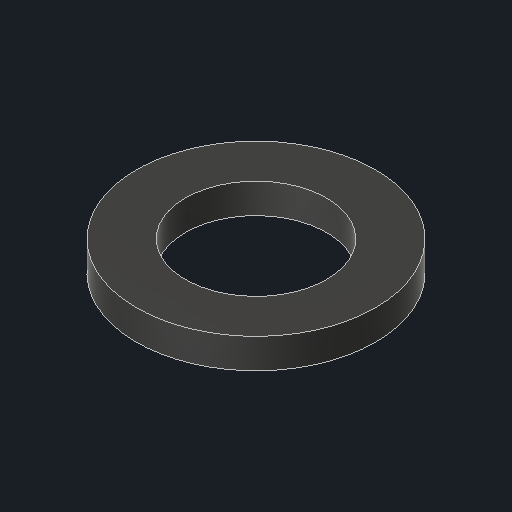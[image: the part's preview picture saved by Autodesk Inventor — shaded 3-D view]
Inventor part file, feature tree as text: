
AUTODESK INVENTOR PART (.ipt)
format: ipt  version: 2023 (Build 270158000, 158)  size: 814,592 bytes
history: native  units: in
note: dims shown in document units (in); Inventor stores cm internally (conversion verified against a paired STEP export)
features: other x39, sketch x4, extrude x3, thread x2, revolve x1, mirror x1
ambient origin geometry x8: Origin, YZ Plane, XZ Plane, XY Plane, X Axis, Y Axis, Z Axis, Center Point
bodies: Body1 (feature_tree)
feature tree (50):
  other  "Table"
  other  "Length = 2"
  other  "Length = 1.4375"
  other  "Length = 2.5"
  other  "Length = 1.75"
  other  "Spacer Type = Nylon Unthreaded Spacer"
  other  "Spacer Size = 4-40"
  other  "Length = 0.125"
  other  "Length = 0.15625"
  other  "Length = 0.1875"
  other  "Length = 0.21875"
  other  "Length = 0.25"
  other  "Length = 0.28125"
  other  "Length = 0.3125"
  other  "Length = 0.34375"
  other  "Length = 0.375"
  other  "Length = 0.40625"
  other  "Length = 0.4375"
  other  "Length = 0.46875"
  other  "Length = 0.5"
  other  "Length = 0.5625"
  other  "Length = 0.625"
  other  "Length = 0.6875"
  other  "Length = 0.75"
  other  "Length = 0.875"
  other  "Length = 1"
  other  "Length = 0.8125"
  other  "Length = 0.9375"
  other  "Length = 1.125"
  other  "Length = 1.1875"
  other  "Length = 1.25"
  other  "Length = 1.3125"
  other  "Length = 1.375"
  other  "Length = 1.5"
  other  "Length = 2.25"
  other  "Spacer Size = 8-32"
  other  "Length = 1.0625"
  other  "Spacer Size = 10-32"
  other  "Spacer Size = 1/4-20"
  revolve  "Revolution1"  [1 undecoded]
  thread  "Thread2"  [1 undecoded]
  thread  "Thread1"  [1 undecoded]
  extrude  "OD Hex"  Depth=0.5in
  extrude  "Hex Round"  TaperAngle=90.0deg  [1 undecoded]
  mirror  "Mirror1"
  extrude  "ID Hex"  Depth=0.375in TaperAngle=0.0deg
  sketch  "Sketch1"  dims[d4=1.0in d5=0.0in d6=1.0in d7=-0.4123in d8=6.0in d9=0.0in d10=0.0in]
  sketch  "Sketch2"  dims[d13=0.2953in d14=0.5in]
  sketch  "Sketch3"  dims[d15=0.0625in d16=90.0deg]
  sketch  "Sketch4"  dims[d17=0.5in d25=0.375in d26=0.0in d27=0.375in d28=0.0in]
note: 4 required parameter values undecoded (feature->parameter linkage not recoverable at this tier; creation-order binding heuristic only, values carry confidence <= 0.55)